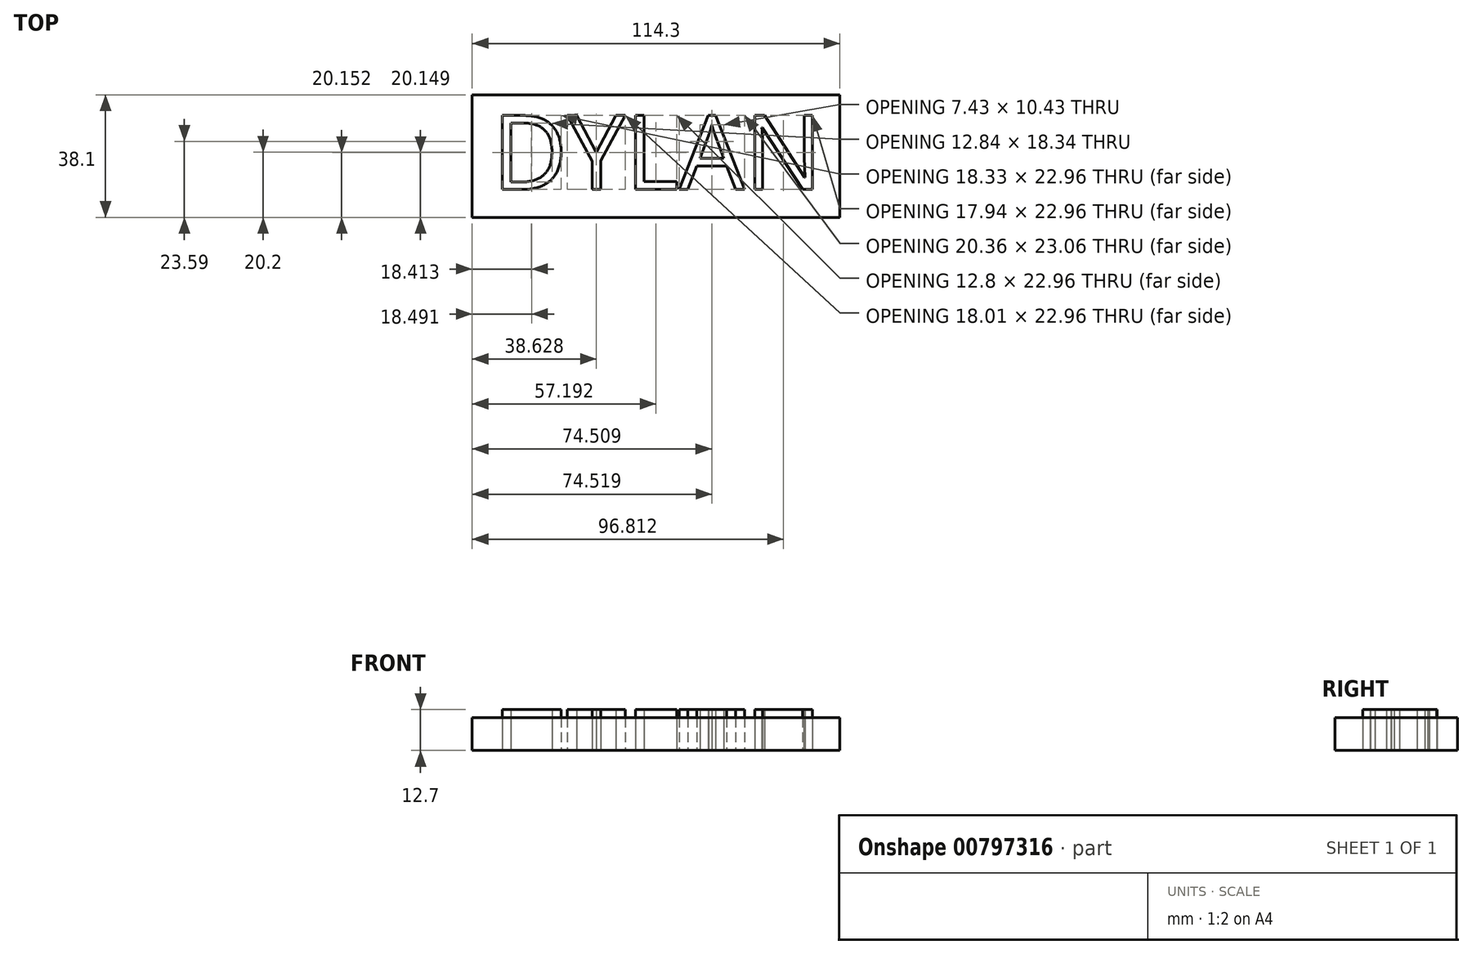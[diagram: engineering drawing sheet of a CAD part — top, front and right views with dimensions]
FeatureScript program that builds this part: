
annotation { "Feature Type Name" : "Feature", "Feature Type Description" : "" }
export const myFeature = defineFeature(function(context is Context, id is Id, definition is map)
    precondition{}
    {
        {
            var Q0;
            Q0=qCreatedBy(makeId("Top.planeOp"),FACE);
            var sketch = newSketch(context, id + "F0", { "sketchPlane" : qUnion([Q0])});
            skLineSegment(sketch, "E0.bottom", {"start": v(-57.15, 19.05) * mm, "end": v(57.15, 19.05) * mm});
            skLineSegment(sketch, "E0.top", {"start": v(-57.15, -19.05) * mm, "end": v(57.15, -19.05) * mm});
            skLineSegment(sketch, "E0.left", {"start": v(-57.15, 19.05) * mm, "end": v(-57.15, -19.05) * mm});
            skLineSegment(sketch, "E0.right", {"start": v(57.15, 19.05) * mm, "end": v(57.15, -19.05) * mm});
            skText(sketch, "E1", { "text": "DYLAN\n", "fontName": "OpenSans-Regular.ttf"});
            const initialGuessF0  = {"E1": [-0.05098, -0.01038, 1, 0, 0.02316]};
            skSetInitialGuess(sketch, initialGuessF0);
            skSolve(sketch);
        }
        {
            var Q0;
            Q0 = qSketchRegion(id + "F0", true);
            var Q1;
            Q1=makeQuery(id+"F0.imprint","IMPRINT",FACE,{"disambiguationData":[TD([[makeQuery(id+"F0.imprint","IMPRINT",EDGE,{"derivedFrom":sQuery(id+"F0.wireOp",EDGE,"E1.sketch_text.stroke-7")}),1.0]])]});
            var Q2;
            Q2=makeQuery(id+"F0.imprint","IMPRINT",FACE,{"disambiguationData":[TD([[makeQuery(id+"F0.imprint","IMPRINT",EDGE,{"derivedFrom":sQuery(id+"F0.wireOp",EDGE,"E1.sketch_text.stroke-37")}),1.0]])]});
            extrude(context, id + "F1", {"entities" : qUnion([Q0, Q1, Q2]), "depth" : 10.16 * mm, "offsetDistance" : 25.4 * mm});
        }
        {
            var Q0;
            Q0=makeQuery(id+"F0.imprint","IMPRINT",FACE,{"disambiguationData":[TD([[makeQuery(id+"F0.imprint","IMPRINT",EDGE,{"derivedFrom":sQuery(id+"F0.wireOp",EDGE,"E1.sketch_text.stroke-29")}),-1.0]])]});
            var Q1;
            Q1=makeQuery(id+"F0.imprint","IMPRINT",FACE,{"disambiguationData":[TD([[makeQuery(id+"F0.imprint","IMPRINT",EDGE,{"derivedFrom":sQuery(id+"F0.wireOp",EDGE,"E1.sketch_text.stroke-42")}),-1.0]])]});
            var Q2;
            Q2=makeQuery(id+"F0.imprint","IMPRINT",FACE,{"disambiguationData":[TD([[makeQuery(id+"F0.imprint","IMPRINT",EDGE,{"derivedFrom":sQuery(id+"F0.wireOp",EDGE,"E1.sketch_text.stroke-23")}),-1.0]])]});
            var Q3;
            Q3=makeQuery(id+"F0.imprint","IMPRINT",FACE,{"disambiguationData":[TD([[makeQuery(id+"F0.imprint","IMPRINT",EDGE,{"derivedFrom":sQuery(id+"F0.wireOp",EDGE,"E1.sketch_text.stroke-14")}),-1.0]])]});
            var Q4;
            Q4=makeQuery(id+"F0.imprint","IMPRINT",FACE,{"disambiguationData":[TD([[makeQuery(id+"F0.imprint","IMPRINT",EDGE,{"derivedFrom":sQuery(id+"F0.wireOp",EDGE,"E1.sketch_text.stroke-0")}),-1.0]])]});
            extrude(context, id + "F2", {"entities" : qUnion([Q0, Q1, Q2, Q3, Q4]), "depth" : 12.7 * mm, "offsetDistance" : 25.4 * mm});
        }
    });
